# Revit family: Deca_Lavatorio_Monte Carlo_L.81
name_source: partatom
category: Plumbing Fixtures
units: mm (PartAtom-declared; Revit-internal decimal feet)

## family parameters
Cut with Voids When Loaded = No
Host = Face
Part Type = Normal
Room Calculation Point = No
Round Connector Dimension = Use Radius
Shared = No

## types (6) — shared parameters
Acompanha o Produto = -
Aprovado por = quattroD
Atendimento ao Cliente = 0800-0117073
Categoria = LAVATORIOS
Composição Anel Vedação = -
Composição Assento = -
Composição Básica = Argila, feldspato, caulim, vidrados e corantes inorgânicos.
Composição Componente = Não Possui
Consumo = -
Cor Interna = -
Cor Secundária = -
Cores Componente = Não Possui
Criado por = quattroD
Código Pai = L.81
Description = Lavatório
Diâmetro Ponto de Esgoto = 25 mm  [stored 0.082021 ft]
Informações Complementares = -
Itens de Instalação = 1601.C; 1601.C.CLI; 1602.C; 1602.C.PLA; 1680.C.100.112; 1682.C.100.112; 1684.C.100.112; C.1.17; CS.1.17; SP.13.01; SP.7.01
Linha = Monte Carlo
Manufacturer = Deca
Norma = NBR-16728-1;NBR-16728-2
Peso Líquido (Kg) = 14.597
Pressão máx. funcionamento = -
Pressão mín. Aquec. Acúmulo = -
Pressão mín. Aquec. Passagem = -
Pressão mín. funcionamento = -
Raio Ponto de Esgoto = 13 mm  [stored 0.0426509 ft]
Saída de Esgoto = Válvula Longa
Segmento = Banheiro Médio
Tipo de dispositivo economizador = -
Tipo de mecanismo utilizado = -
Tipo de rosca de entrada = -
Tipo de rosca de saída = -
URL = www.deca.com.br
Vazão na Pressão máx. (L/min) = -
Vazão na Pressão mín. (L/min) = -
zero-valued in all types: Default Elevation, WFU

## per-type parameters (varying)
| type | Combinação | Cor Principal | Material | Model |
| L.81.17_Branco_C.1.17 | Deca_Coluna para lavatório_Coluna Univ. Médio_C.1 : C.1.17_Branco | Branco | Deca_Branco | L.81.17 |
| L.81.37_Creme_C.1.37 | Deca_Coluna para lavatório_Coluna Univ. Médio_C.1 : C.1.37_Creme | Creme | Deca_Creme | L.81.37 |
| L.81.17_Branco_CS.1.17 | Deca_Coluna suspensa para lavatório_Coluna Univ. Médio_CS.1 : CS.1.17_Branco | Branco | Deca_Branco | L.81.17 |
| L.81.37_Creme_CS.1.37 | Deca_Coluna suspensa para lavatório_Coluna Univ. Médio_CS.1 : CS.1.37_Creme | Creme | Deca_Creme | L.81.37 |
| L.81.95_Ébano_CS.1.95 | Deca_Coluna suspensa para lavatório_Coluna Univ. Médio_CS.1 : CS.1.95_Ébano | Ébano | Deca_Ébano | L.81.95 |
| L.81.95_Ébano_C.1.95 | Deca_Coluna para lavatório_Coluna Univ. Médio_C.1 : C.1.95_Ébano | Ébano | Deca_Ébano | L.81.95 |

note: [stored X ft] marks values corroborated as IEEE doubles in the binary element streams (Revit-internal decimal feet)

## geometry (parser evidence)
native form markers: Sweep x7
no freeform markers — native parametric forms only
